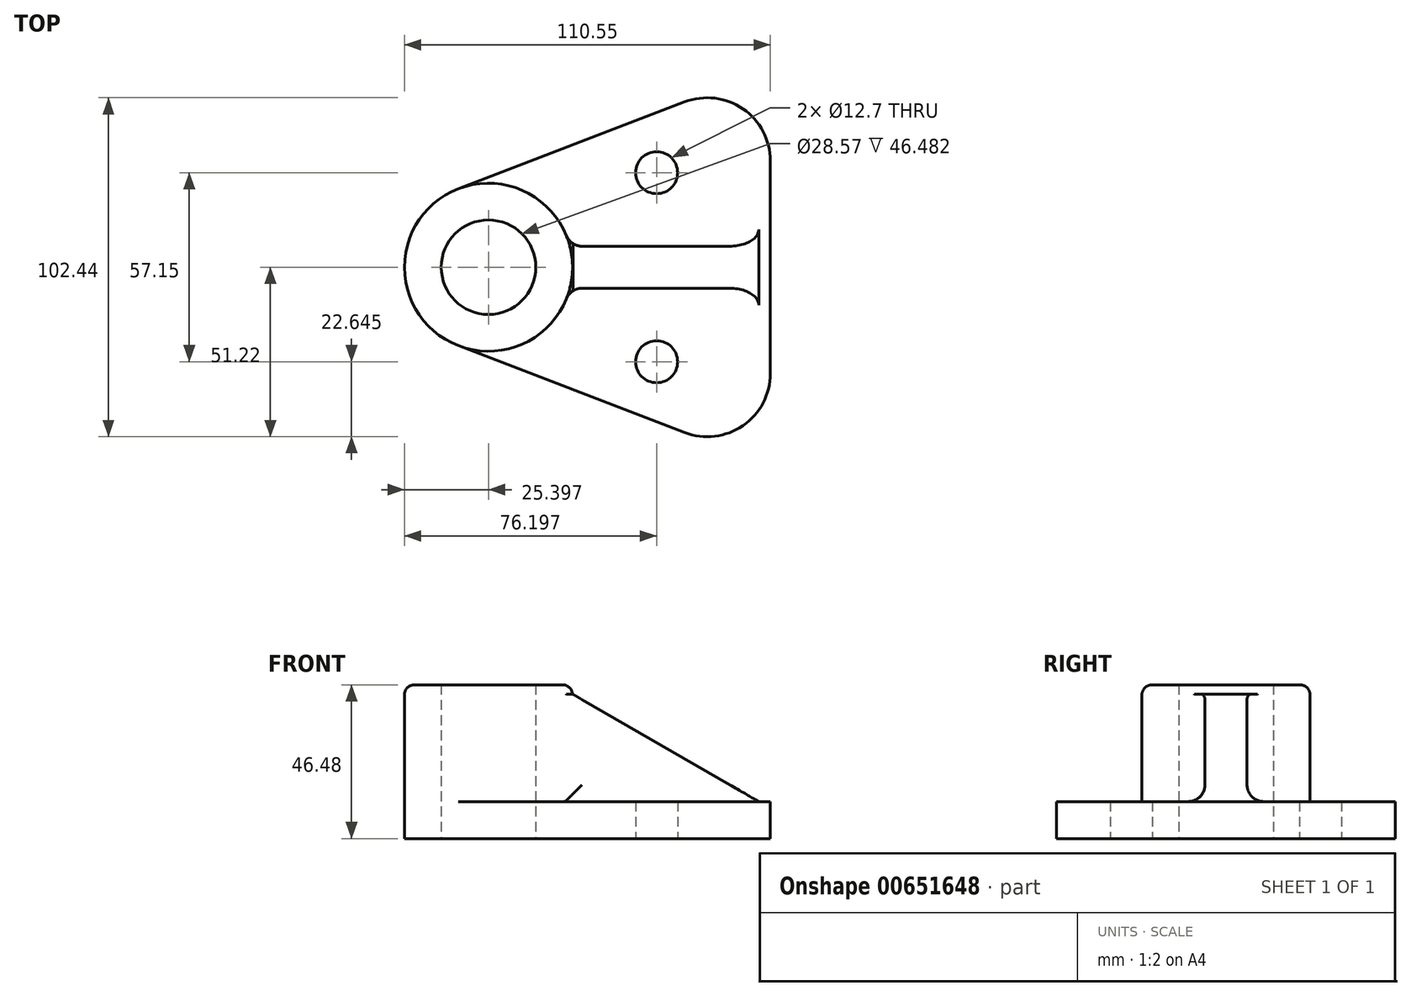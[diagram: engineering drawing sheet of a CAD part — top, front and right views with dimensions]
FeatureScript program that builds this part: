
annotation { "Feature Type Name" : "Feature", "Feature Type Description" : "" }
export const myFeature = defineFeature(function(context is Context, id is Id, definition is map)
    precondition{}
    {
        {
            var Q0;
            Q0=qCreatedBy(makeId("Top.planeOp"),FACE);
            var sketch = newSketch(context, id + "F0", { "sketchPlane" : qUnion([Q0])});
            skPoint(sketch, "E0.middle", {"position": v(0, 0) * mm});
            skCircle(sketch, "E1", {"center": v(-85.15, 0) * mm, "radius": 25.4 * mm});
            skLineSegment(sketch, "E2", {"start": v(-94.25, 23.71) * mm, "end": v(0, 59.88) * mm});
            skLineSegment(sketch, "E3", {"start": v(-94.25, -23.71) * mm, "end": v(0, -59.88) * mm});
            skCircle(sketch, "E4", {"center": v(-34.35, -28.58) * mm, "radius": 6.35 * mm});
            skCircle(sketch, "E5.MirrorC", {"center": v(-34.35, 28.58) * mm, "radius": 6.35 * mm});
            skLineSegment(sketch, "E6", {"start": v(0, -59.88) * mm, "end": v(0, 59.88) * mm});
            skCircle(sketch, "E7", {"center": v(-85.15, 0) * mm, "radius": 14.29 * mm});
            skSolve(sketch);
        }
        {
            var Q0;
            Q0=makeQuery(id+"F0.imprint","IMPRINT",FACE,{"disambiguationData":[TD([[makeQuery(id+"F0.imprint","IMPRINT",EDGE,{"derivedFrom":sQuery(id+"F0.wireOp",EDGE,"E7")}),-1.0]])]});
            extrude(context, id + "F1", {"entities" : qUnion([Q0]), "depth" : 46.48 * mm, "offsetDistance" : 25.4 * mm});
        }
        {
            var Q0;
            {var subQ0=sQuery(id+"F0.wireOp",EDGE,"E3");Q0=makeQuery(id+"F0.imprint","IMPRINT",FACE,{"disambiguationData":[TD([[makeQuery(id+"F0.imprint","IMPRINT",EDGE,{"derivedFrom":subQ0}),1.0]])]});}
            var Q1;
            {var subQ1=sQuery(id+"F0.wireOp",EDGE,"E2");Q1=makeQuery(id+"F0.imprint","IMPRINT",FACE,{"disambiguationData":[TD([[makeQuery(id+"F0.imprint","IMPRINT",EDGE,{"derivedFrom":subQ1}),-1.0]])]});}
            extrude(context, id + "F2", {"entities" : qUnion([Q0, Q1]), "operationType" : NewBodyOperationType.ADD, "depth" : 11.18 * mm, "offsetDistance" : 25.4 * mm});
        }
        {
            var Q0;
            Q0=qCreatedBy(makeId("Front.planeOp"),FACE);
            var sketch = newSketch(context, id + "F3", { "sketchPlane" : qUnion([Q0])});
            skLineSegment(sketch, "E8", {"start": v(-59.62, 11.08) * mm, "end": v(-3.3, 11.08) * mm});
            skLineSegment(sketch, "E9", {"start": v(-59.62, 43.6) * mm, "end": v(-3.3, 11.08) * mm});
            skLineSegment(sketch, "E10", {"start": v(-59.62, 11.08) * mm, "end": v(-69.36, 11.08) * mm});
            skLineSegment(sketch, "E11", {"start": v(-69.36, 11.08) * mm, "end": v(-69.36, 43.68) * mm});
            skLineSegment(sketch, "E12", {"start": v(-69.36, 43.68) * mm, "end": v(-59.62, 43.6) * mm});
            skSolve(sketch);
        }
        {
            var Q0;
            Q0 = qSketchRegion(id + "F3", true);
            extrude(context, id + "F4", {"entities" : qUnion([Q0]), "operationType" : NewBodyOperationType.ADD, "endBound" : BoundingType.SYMMETRIC, "depth" : 12.7 * mm, "offsetDistance" : 25.4 * mm});
        }
        {
            var Q0;
            Q0=makeQuery(id+"F1.opExtrude","CAP_EDGE",EDGE,{"disambiguationData":[OSD([sQuery(id+"F0.wireOp",EDGE,"E1")])],"isStart":false});
            fillet(context, id + "F5", {"entities" : qUnion([Q0]), "radius" : 3.05 * mm, "tangentPropagation" : true, "allowEdgeOverflow" : false});
        }
        {
            var Q0;
            Q0=makeQuery(id+"F2.opExtrude","CAP_EDGE",EDGE,{"disambiguationData":[OSD([sQuery(id+"F0.wireOp",EDGE,"E1")])],"isStart":false});
            var Q1;
            Q1=makeQuery(id+"F4.boolean.opBoolean","INTERSECT",EDGE,{"derivedFrom":[makeQuery(id+"F2.opExtrude","CAP_FACE",FACE,{"disambiguationData":[OSD([sQuery(id+"F0.wireOp",EDGE,"E1"),sQuery(id+"F0.wireOp",EDGE,"E2"),sQuery(id+"F0.wireOp",EDGE,"E3"),sQuery(id+"F0.wireOp",EDGE,"E4"),sQuery(id+"F0.wireOp",EDGE,"E5.MirrorC"),sQuery(id+"F0.wireOp",EDGE,"E6")])],"isStart":false}),makeQuery(id+"F4.opExtrude","CAP_FACE",FACE,{"disambiguationData":[OSD([sQuery(id+"F3.wireOp",EDGE,"E8"),sQuery(id+"F3.wireOp",EDGE,"E9"),sQuery(id+"F3.wireOp",EDGE,"E10"),sQuery(id+"F3.wireOp",EDGE,"E11"),sQuery(id+"F3.wireOp",EDGE,"E12")])],"isStart":false})]});
            var Q2;
            Q2=makeQuery(id+"F4.boolean.opBoolean","INTERSECT",EDGE,{"derivedFrom":[makeQuery(id+"F1.opExtrude","SWEPT_FACE",FACE,{"disambiguationData":[OSD([sQuery(id+"F0.wireOp",EDGE,"E1")])]}),makeQuery(id+"F4.opExtrude","CAP_FACE",FACE,{"disambiguationData":[OSD([sQuery(id+"F3.wireOp",EDGE,"E8"),sQuery(id+"F3.wireOp",EDGE,"E9"),sQuery(id+"F3.wireOp",EDGE,"E10"),sQuery(id+"F3.wireOp",EDGE,"E11"),sQuery(id+"F3.wireOp",EDGE,"E12")])],"isStart":false})]});
            var Q3;
            Q3=makeQuery(id+"F4.boolean.opBoolean","INTERSECT",EDGE,{"derivedFrom":[makeQuery(id+"F2.opExtrude","CAP_FACE",FACE,{"disambiguationData":[OSD([sQuery(id+"F0.wireOp",EDGE,"E1"),sQuery(id+"F0.wireOp",EDGE,"E2"),sQuery(id+"F0.wireOp",EDGE,"E3"),sQuery(id+"F0.wireOp",EDGE,"E4"),sQuery(id+"F0.wireOp",EDGE,"E5.MirrorC"),sQuery(id+"F0.wireOp",EDGE,"E6")])],"isStart":false}),makeQuery(id+"F4.opExtrude","CAP_FACE",FACE,{"disambiguationData":[OSD([sQuery(id+"F3.wireOp",EDGE,"E8"),sQuery(id+"F3.wireOp",EDGE,"E9"),sQuery(id+"F3.wireOp",EDGE,"E10"),sQuery(id+"F3.wireOp",EDGE,"E11"),sQuery(id+"F3.wireOp",EDGE,"E12")])],"isStart":true})]});
            var Q4;
            Q4=makeQuery(id+"F4.boolean.opBoolean","INTERSECT",EDGE,{"derivedFrom":[makeQuery(id+"F1.opExtrude","SWEPT_FACE",FACE,{"disambiguationData":[OSD([sQuery(id+"F0.wireOp",EDGE,"E1")])]}),makeQuery(id+"F4.opExtrude","CAP_FACE",FACE,{"disambiguationData":[OSD([sQuery(id+"F3.wireOp",EDGE,"E8"),sQuery(id+"F3.wireOp",EDGE,"E9"),sQuery(id+"F3.wireOp",EDGE,"E10"),sQuery(id+"F3.wireOp",EDGE,"E11"),sQuery(id+"F3.wireOp",EDGE,"E12")])],"isStart":true})]});
            fillet(context, id + "F6", {"entities" : qUnion([Q0, Q1, Q2, Q3, Q4]), "radius" : 5.08 * mm, "tangentPropagation" : true, "allowEdgeOverflow" : false});
        }
        {
            var Q0;
            Q0=makeQuery(id+"F2.opExtrude","SWEPT_EDGE",EDGE,{"disambiguationData":[OSD([sQuery(id+"F0.wireOp",EDGE,"E3"),sQuery(id+"F0.wireOp",EDGE,"E6")])]});
            var Q1;
            Q1=makeQuery(id+"F2.opExtrude","SWEPT_EDGE",EDGE,{"disambiguationData":[OSD([sQuery(id+"F0.wireOp",EDGE,"E2"),sQuery(id+"F0.wireOp",EDGE,"E6")])]});
            fillet(context, id + "F7", {"entities" : qUnion([Q0, Q1]), "radius" : 19.05 * mm, "tangentPropagation" : true, "allowEdgeOverflow" : false});
        }
    });
